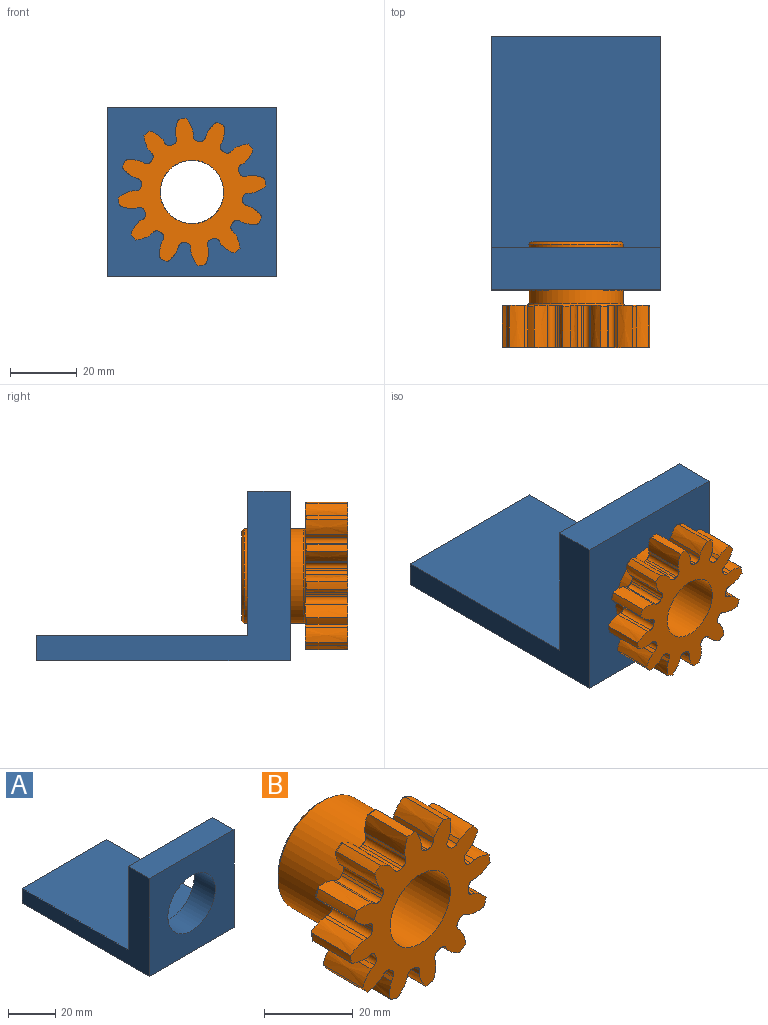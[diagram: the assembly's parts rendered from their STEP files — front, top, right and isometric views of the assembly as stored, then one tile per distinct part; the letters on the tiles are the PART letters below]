
ASSEMBLY  parts=2 mates=1
PART A: 9 faces, bbox 50.8x76.2x50.8 mm
  f0: plane 76.2x50.8mm, normal (1,0,0), area 1129mm2, adj f2,f3,f4,f5,f6,f7
  f1: plane 76.2x50.8mm, normal (-1,0,0), area 1129mm2, adj f2,f3,f4,f5,f6,f7
  f2: plane 50.8x43.18mm, normal (0,1,0), area 1557.9mm2, adj f0,f1,f3,f6,f8
  f3: plane 50.8x12.7mm, normal (0,0,1), area 645.2mm2, adj f0,f1,f2,f4
  f4: plane 50.8x50.8mm, normal (0,-1,0), area 1945mm2, adj f0,f1,f3,f5,f8
  f5: plane 76.2x50.8mm, normal (0,0,-1), area 3871mm2, adj f0,f1,f4,f7
  f6: plane 63.5x50.8mm, normal (0,0,1), area 3225.8mm2, adj f0,f1,f2,f7
  f7: plane 50.8x7.62mm, normal (0,1,0), area 387.1mm2, adj f0,f1,f5,f6
  f8: cylinder r=14.22mm len=28.45mm, axis (0,-1,0), area 1135mm2, adj f2,f4
PART B: 116 faces, bbox 44.5x31.8x44.5 mm
  f0: cylinder r=22.23mm len=12.26mm, axis (0,-1,0), area 27.9mm2, adj f86,f89,f97,f115
  f1: cylinder r=22.23mm len=12.26mm, axis (0,-1,0), area 27.9mm2, adj f79,f82,f98,f115
  f2: cylinder r=22.23mm len=12.26mm, axis (0,-1,0), area 27.9mm2, adj f72,f75,f99,f115
  f3: cylinder r=22.23mm len=12.26mm, axis (0,-1,0), area 27.9mm2, adj f65,f68,f100,f115
  f4: cylinder r=22.23mm len=12.26mm, axis (0,-1,0), area 27.9mm2, adj f58,f61,f101,f115
  f5: cylinder r=22.23mm len=12.26mm, axis (0,-1,0), area 27.9mm2, adj f51,f54,f102,f115
  f6: cylinder r=22.23mm len=12.26mm, axis (0,-1,0), area 27.9mm2, adj f44,f47,f103,f115
  f7: cylinder r=22.23mm len=12.26mm, axis (0,-1,0), area 27.9mm2, adj f37,f40,f104,f115
  f8: cylinder r=22.23mm len=12.26mm, axis (0,-1,0), area 27.9mm2, adj f30,f33,f105,f115
  f9: cylinder r=22.23mm len=12.26mm, axis (0,-1,0), area 27.9mm2, adj f23,f26,f106,f115
  f10: cylinder r=22.23mm len=12.26mm, axis (0,-1,0), area 27.9mm2, adj f15,f19,f107,f115
  f11: cylinder r=22.23mm len=12.26mm, axis (0,-1,0), area 27.9mm2, adj f16,f93,f112,f115
  f12: plane 12.7x1.09mm, normal (-0.97,0,0.26), area 14.3mm2, adj f16,f17,f108,f115
  f13: cylinder r=15.38mm len=12.7mm, axis (0,-1,0), area 9.1mm2, adj f17,f18,f108,f115
  f14: plane 12.7x1.12mm, normal (1,0,0), area 14.3mm2, adj f15,f18,f108,f115
  f15: extruded ~12.7x4.26mm, area 60.8mm2, adj f10,f14,f107,f108,f115
  f16: extruded ~12.7x3.57mm, area 60.8mm2, adj f11,f12,f108,f112,f115
  f17: cylinder r=1.5mm len=12.7mm, axis (0,-1,0), area 27.8mm2, adj f12,f13,f108,f115
  f18: cylinder r=1.5mm len=12.7mm, axis (0,-1,0), area 27.8mm2, adj f13,f14,f108,f115
  f19: extruded ~12.7x4.65mm, area 60.8mm2, adj f10,f20,f107,f108,f115
  f20: plane 12.7x1.09mm, normal (-0.97,0,-0.26), area 14.3mm2, adj f19,f21,f108,f115
  f21: cylinder r=1.5mm len=12.7mm, axis (0,-1,0), area 27.8mm2, adj f20,f22,f108,f115
  f22: cylinder r=15.38mm len=12.7mm, axis (0,-1,0), area 9.1mm2, adj f21,f25,f108,f115
  f23: extruded ~12.7x3.93mm, area 60.8mm2, adj f9,f24,f106,f108,f115
  f24: plane 12.7x0.97mm, normal (0.87,0,0.5), area 14.3mm2, adj f23,f25,f108,f115
  f25: cylinder r=1.5mm len=12.7mm, axis (0,-1,0), area 27.8mm2, adj f22,f24,f108,f115
  f26: extruded ~12.7x4.48mm, area 60.8mm2, adj f9,f27,f106,f108,f115
  f27: plane 12.7x0.79mm, normal (-0.71,0,-0.71), area 14.3mm2, adj f26,f28,f108,f115
  f28: cylinder r=1.5mm len=12.7mm, axis (0,-1,0), area 27.8mm2, adj f27,f29,f108,f115
  f29: cylinder r=15.38mm len=12.7mm, axis (0,-1,0), area 9.1mm2, adj f28,f32,f108,f115
  f30: extruded ~12.7x4.73mm, area 60.8mm2, adj f8,f31,f105,f108,f115
  f31: plane 12.7x0.97mm, normal (0.5,0,0.87), area 14.3mm2, adj f30,f32,f108,f115
  f32: cylinder r=1.5mm len=12.7mm, axis (0,-1,0), area 27.8mm2, adj f29,f31,f108,f115
  f33: extruded ~12.7x3.57mm, area 60.8mm2, adj f8,f34,f105,f108,f115
  f34: plane 12.7x1.09mm, normal (-0.26,0,-0.97), area 14.3mm2, adj f33,f35,f108,f115
  f35: cylinder r=1.5mm len=12.7mm, axis (0,-1,0), area 27.8mm2, adj f34,f36,f108,f115
  f36: cylinder r=15.38mm len=12.7mm, axis (0,-1,0), area 9.1mm2, adj f35,f39,f108,f115
  f37: extruded ~12.7x4.26mm, area 60.8mm2, adj f7,f38,f104,f108,f115
  f38: plane 12.7x1.12mm, normal (0,0,1), area 14.3mm2, adj f37,f39,f108,f115
  f39: cylinder r=1.5mm len=12.7mm, axis (0,-1,0), area 27.8mm2, adj f36,f38,f108,f115
  f40: extruded ~12.7x4.65mm, area 60.8mm2, adj f7,f41,f104,f108,f115
  f41: plane 12.7x1.09mm, normal (0.26,0,-0.97), area 14.3mm2, adj f40,f42,f108,f115
  f42: cylinder r=1.5mm len=12.7mm, axis (0,-1,0), area 27.8mm2, adj f41,f43,f108,f115
  f43: cylinder r=15.38mm len=12.7mm, axis (0,-1,0), area 9.1mm2, adj f42,f46,f108,f115
  f44: extruded ~12.7x3.93mm, area 60.8mm2, adj f6,f45,f103,f108,f115
  f45: plane 12.7x0.97mm, normal (-0.5,0,0.87), area 14.3mm2, adj f44,f46,f108,f115
  f46: cylinder r=1.5mm len=12.7mm, axis (0,-1,0), area 27.8mm2, adj f43,f45,f108,f115
  f47: extruded ~12.7x4.48mm, area 60.8mm2, adj f6,f48,f103,f108,f115
  f48: plane 12.7x0.79mm, normal (0.71,0,-0.71), area 14.3mm2, adj f47,f49,f108,f115
  f49: cylinder r=1.5mm len=12.7mm, axis (0,-1,0), area 27.8mm2, adj f48,f50,f108,f115
  f50: cylinder r=15.38mm len=12.7mm, axis (0,-1,0), area 9.1mm2, adj f49,f53,f108,f115
  f51: extruded ~12.7x4.73mm, area 60.8mm2, adj f5,f52,f102,f108,f115
  f52: plane 12.7x0.97mm, normal (-0.87,0,0.5), area 14.3mm2, adj f51,f53,f108,f115
  f53: cylinder r=1.5mm len=12.7mm, axis (0,-1,0), area 27.8mm2, adj f50,f52,f108,f115
  f54: extruded ~12.7x3.57mm, area 60.8mm2, adj f5,f55,f102,f108,f115
  f55: plane 12.7x1.09mm, normal (0.97,0,-0.26), area 14.3mm2, adj f54,f56,f108,f115
  f56: cylinder r=1.5mm len=12.7mm, axis (0,-1,0), area 27.8mm2, adj f55,f57,f108,f115
  f57: cylinder r=15.38mm len=12.7mm, axis (0,-1,0), area 9.1mm2, adj f56,f60,f108,f115
  f58: extruded ~12.7x4.26mm, area 60.8mm2, adj f4,f59,f101,f108,f115
  f59: plane 12.7x1.12mm, normal (-1,0,0), area 14.3mm2, adj f58,f60,f108,f115
  f60: cylinder r=1.5mm len=12.7mm, axis (0,-1,0), area 27.8mm2, adj f57,f59,f108,f115
  f61: extruded ~12.7x4.65mm, area 60.8mm2, adj f4,f62,f101,f108,f115
  f62: plane 12.7x1.09mm, normal (0.97,0,0.26), area 14.3mm2, adj f61,f63,f108,f115
  f63: cylinder r=1.5mm len=12.7mm, axis (0,-1,0), area 27.8mm2, adj f62,f64,f108,f115
  f64: cylinder r=15.38mm len=12.7mm, axis (0,-1,0), area 9.1mm2, adj f63,f67,f108,f115
  f65: extruded ~12.7x3.93mm, area 60.8mm2, adj f3,f66,f100,f108,f115
  f66: plane 12.7x0.97mm, normal (-0.87,0,-0.5), area 14.3mm2, adj f65,f67,f108,f115
  f67: cylinder r=1.5mm len=12.7mm, axis (0,-1,0), area 27.8mm2, adj f64,f66,f108,f115
  f68: extruded ~12.7x4.48mm, area 60.8mm2, adj f3,f69,f100,f108,f115
  f69: plane 12.7x0.79mm, normal (0.71,0,0.71), area 14.3mm2, adj f68,f70,f108,f115
  f70: cylinder r=1.5mm len=12.7mm, axis (0,-1,0), area 27.8mm2, adj f69,f71,f108,f115
  f71: cylinder r=15.38mm len=12.7mm, axis (0,-1,0), area 9.1mm2, adj f70,f74,f108,f115
  f72: extruded ~12.7x4.73mm, area 60.8mm2, adj f2,f73,f99,f108,f115
  f73: plane 12.7x0.97mm, normal (-0.5,0,-0.87), area 14.3mm2, adj f72,f74,f108,f115
  f74: cylinder r=1.5mm len=12.7mm, axis (0,-1,0), area 27.8mm2, adj f71,f73,f108,f115
  f75: extruded ~12.7x3.57mm, area 60.8mm2, adj f2,f76,f99,f108,f115
  f76: plane 12.7x1.09mm, normal (0.26,0,0.97), area 14.3mm2, adj f75,f77,f108,f115
  f77: cylinder r=1.5mm len=12.7mm, axis (0,-1,0), area 27.8mm2, adj f76,f78,f108,f115
  f78: cylinder r=15.38mm len=12.7mm, axis (0,-1,0), area 9.1mm2, adj f77,f81,f108,f115
  f79: extruded ~12.7x4.26mm, area 60.8mm2, adj f1,f80,f98,f108,f115
  f80: plane 12.7x1.12mm, normal (0,0,-1), area 14.3mm2, adj f79,f81,f108,f115
  f81: cylinder r=1.5mm len=12.7mm, axis (0,-1,0), area 27.8mm2, adj f78,f80,f108,f115
  f82: extruded ~12.7x4.65mm, area 60.8mm2, adj f1,f83,f98,f108,f115
  f83: plane 12.7x1.09mm, normal (-0.26,0,0.97), area 14.3mm2, adj f82,f84,f108,f115
  f84: cylinder r=1.5mm len=12.7mm, axis (0,-1,0), area 27.8mm2, adj f83,f85,f108,f115
  f85: cylinder r=15.38mm len=12.7mm, axis (0,-1,0), area 9.1mm2, adj f84,f88,f108,f115
  f86: extruded ~12.7x3.93mm, area 60.8mm2, adj f0,f87,f97,f108,f115
  f87: plane 12.7x0.97mm, normal (0.5,0,-0.87), area 14.3mm2, adj f86,f88,f108,f115
  f88: cylinder r=1.5mm len=12.7mm, axis (0,-1,0), area 27.8mm2, adj f85,f87,f108,f115
  f89: extruded ~12.7x4.48mm, area 60.8mm2, adj f0,f90,f97,f108,f115
  f90: plane 12.7x0.79mm, normal (-0.71,0,0.71), area 14.3mm2, adj f89,f91,f108,f115
  f91: cylinder r=1.5mm len=12.7mm, axis (0,-1,0), area 27.8mm2, adj f90,f92,f108,f115
  f92: cylinder r=15.38mm len=12.7mm, axis (0,-1,0), area 9.1mm2, adj f91,f95,f108,f115
  f93: extruded ~12.7x4.73mm, area 60.8mm2, adj f11,f94,f108,f112,f115
  f94: plane 12.7x0.97mm, normal (0.87,0,-0.5), area 14.3mm2, adj f93,f95,f108,f115
  f95: cylinder r=1.5mm len=12.7mm, axis (0,-1,0), area 27.8mm2, adj f92,f94,f108,f115
  f96: cylinder r=9.53mm len=31.04mm, axis (0,-1,0), area 1857.6mm2, adj f113,f115
  f97: torus R=21.78mm, axis (0,-1,0), area 1.7mm2, adj f0,f86,f89,f108
  f98: torus R=21.78mm, axis (0,-1,0), area 1.7mm2, adj f1,f79,f82,f108
  f99: torus R=21.78mm, axis (0,-1,0), area 1.7mm2, adj f2,f72,f75,f108
  f100: torus R=21.78mm, axis (0,-1,0), area 1.7mm2, adj f3,f65,f68,f108
  f101: torus R=21.78mm, axis (0,-1,0), area 1.7mm2, adj f4,f58,f61,f108
  f102: torus R=21.78mm, axis (0,-1,0), area 1.7mm2, adj f5,f51,f54,f108
  f103: torus R=21.78mm, axis (0,-1,0), area 1.7mm2, adj f6,f44,f47,f108
  f104: torus R=21.78mm, axis (0,-1,0), area 1.7mm2, adj f7,f37,f40,f108
  f105: torus R=21.78mm, axis (0,-1,0), area 1.7mm2, adj f8,f30,f33,f108
  f106: torus R=21.78mm, axis (0,-1,0), area 1.7mm2, adj f9,f23,f26,f108
  f107: torus R=21.78mm, axis (0,-1,0), area 1.7mm2, adj f10,f15,f19,f108
  f108: plane 43.64x43.64mm, normal (0,1,0), area 432.8mm2, adj f12,f13,f14,f15,f16,f17,f18,f19
  f109: cylinder r=14.22mm len=28.45mm, axis (0,-1,0), area 1599.2mm2, adj f111,f114
  f110: plane 27.03x27.03mm, normal (0,1,0), area 244.5mm2, adj f113,f114
  f111: torus R=14.67mm, axis (0,-1,0), area 63.1mm2, adj f108,f109
  f112: torus R=21.78mm, axis (0,-1,0), area 1.7mm2, adj f11,f16,f93,f108
  f113: cone r=10.24mm half-angle=45deg, axis (0,1,0), area 62.4mm2, adj f96,f110
  f114: cone r=14.22mm half-angle=45deg, axis (0,-1,0), area 87.6mm2, adj f109,f110
  f115: plane 44.53x44.53mm, normal (0,-1,0), area 837.4mm2, adj f0,f1,f2,f3,f4,f5,f6,f7
PLACE A t=(-76.87,-12.17,-27.33)mm
PLACE B t=(-51.47,-105.6,-1.93)mm
MATE cylindrical B.f0 <-> A.f8  axis (0,-1,0) through (-51.47,-58.11,-1.93)mm
